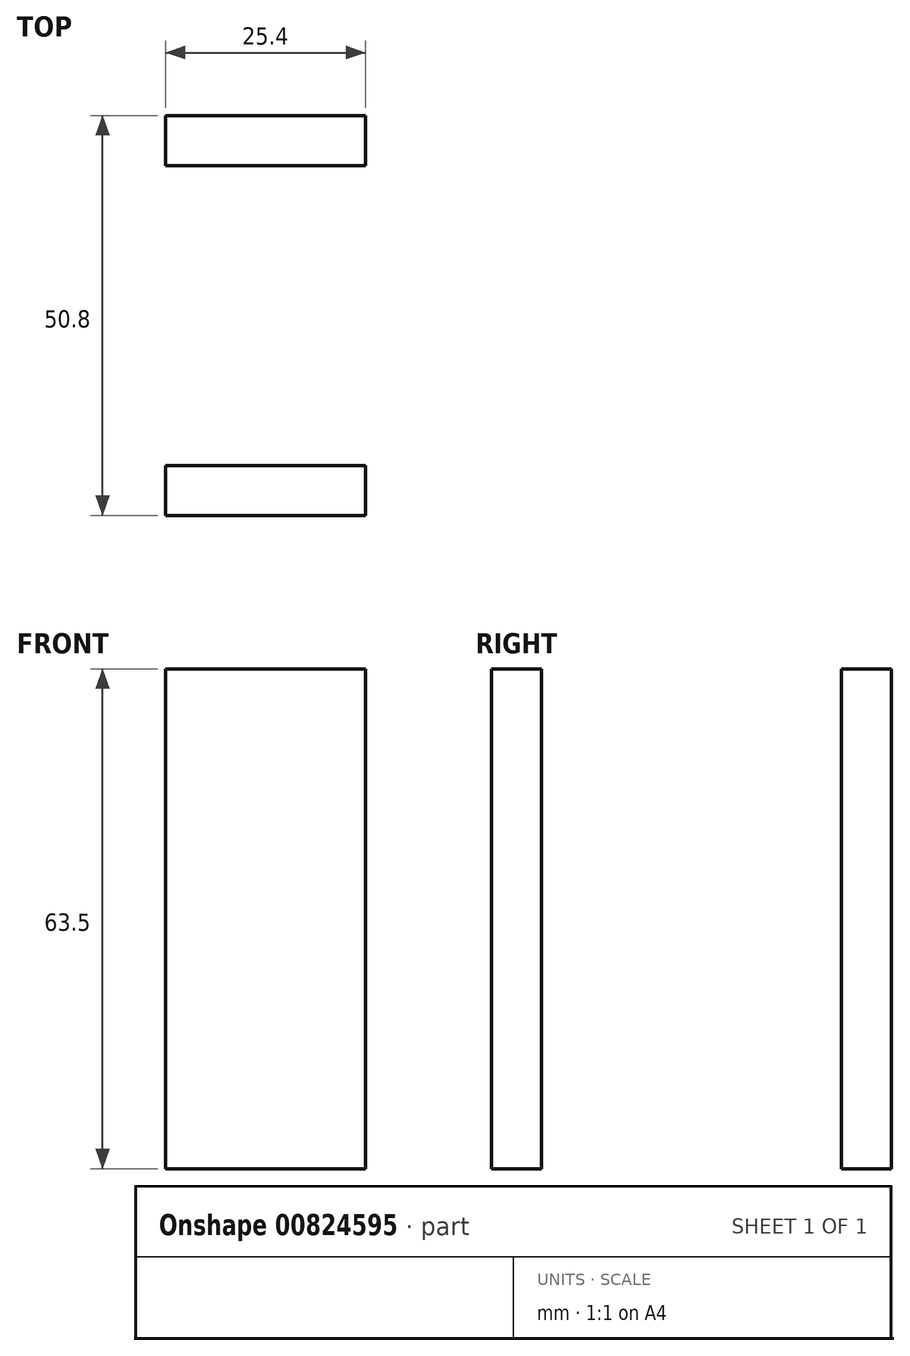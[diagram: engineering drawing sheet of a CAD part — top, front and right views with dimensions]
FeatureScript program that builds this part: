
annotation { "Feature Type Name" : "Feature", "Feature Type Description" : "" }
export const myFeature = defineFeature(function(context is Context, id is Id, definition is map)
    precondition{}
    {
        {
            var Q0;
            Q0=qCreatedBy(makeId("Right.planeOp"),FACE);
            var sketch = newSketch(context, id + "F0", { "sketchPlane" : qUnion([Q0])});
            skLineSegment(sketch, "E0", {"start": v(0, 0) * mm, "end": v(50.8, 0) * mm});
            skLineSegment(sketch, "E1", {"start": v(0, 0) * mm, "end": v(0, -76.2) * mm});
            skLineSegment(sketch, "E2", {"start": v(0, -76.2) * mm, "end": v(50.8, -76.2) * mm});
            skLineSegment(sketch, "E3", {"start": v(50.8, 0) * mm, "end": v(50.8, -76.2) * mm});
            skSolve(sketch);
        }
        {
            var Q0;
            Q0=makeQuery(id+"F0.imprint","IMPRINT",FACE,{"disambiguationData":[TD([[makeQuery(id+"F0.imprint","IMPRINT",EDGE,{"derivedFrom":sQuery(id+"F0.wireOp",EDGE,"E0")}),-1.0]])]});
            extrude(context, id + "F1", {"entities" : qUnion([Q0]), "depth" : 38.1 * mm, "offsetDistance" : 25.4 * mm});
        }
        {
            var Q0;
            Q0=makeQuery(id+"F1.opExtrude","SWEPT_FACE",FACE,{"disambiguationData":[OSD([sQuery(id+"F0.wireOp",EDGE,"E2")])]});
            var sketch = newSketch(context, id + "F2", { "sketchPlane" : qUnion([Q0])});
            skLineSegment(sketch, "E4", {"start": v(0, 0) * mm, "end": v(0, -50.8) * mm});
            skLineSegment(sketch, "E5", {"start": v(0, 0) * mm, "end": v(0, -6.35) * mm});
            skLineSegment(sketch, "E6", {"start": v(0, -6.35) * mm, "end": v(31.75, -6.35) * mm});
            skLineSegment(sketch, "E7", {"start": v(31.75, -6.35) * mm, "end": v(31.75, -44.45) * mm});
            skLineSegment(sketch, "E8", {"start": v(38.1, -50.8) * mm, "end": v(38.1, -44.45) * mm});
            skLineSegment(sketch, "E9", {"start": v(38.1, -44.45) * mm, "end": v(38.1, -50.8) * mm});
            skLineSegment(sketch, "E10", {"start": v(31.75, -44.45) * mm, "end": v(6.35, -44.45) * mm});
            skLineSegment(sketch, "E11", {"start": v(0, -6.35) * mm, "end": v(6.35, -6.35) * mm});
            skLineSegment(sketch, "E12", {"start": v(6.35, -6.35) * mm, "end": v(6.35, -44.45) * mm});
            skSolve(sketch);
        }
        {
            var Q0;
            Q0=makeQuery(id+"F2.imprint","IMPRINT",FACE,{"disambiguationData":[TD([[makeQuery(id+"F2.imprint","IMPRINT",EDGE,{"derivedFrom":sQuery(id+"F2.wireOp",EDGE,"E6")}),-1.0]])]});
            extrude(context, id + "F3", {"entities" : qUnion([Q0]), "operationType" : NewBodyOperationType.REMOVE, "oppositeDirection" : true, "depth" : 63.5 * mm, "offsetDistance" : 25.4 * mm});
        }
        {
            var Q0;
            Q0=makeQuery(id+"F1.opExtrude","SWEPT_FACE",FACE,{"disambiguationData":[OSD([sQuery(id+"F0.wireOp",EDGE,"E3")])]});
            var sketch = newSketch(context, id + "F4", { "sketchPlane" : qUnion([Q0])});
            skLineSegment(sketch, "E13", {"start": v(-38.1, -76.2) * mm, "end": v(0, -76.2) * mm});
            skLineSegment(sketch, "E14", {"start": v(-38.1, -76.2) * mm, "end": v(-31.75, -76.2) * mm});
            skLineSegment(sketch, "E15", {"start": v(0, -76.2) * mm, "end": v(-6.35, -76.2) * mm});
            skLineSegment(sketch, "E16", {"start": v(-31.75, -76.2) * mm, "end": v(-31.75, -12.7) * mm});
            skLineSegment(sketch, "E17", {"start": v(-38.1, -76.2) * mm, "end": v(-38.1, 0) * mm});
            skLineSegment(sketch, "E18", {"start": v(-31.75, -12.7) * mm, "end": v(-6.35, -12.7) * mm});
            skLineSegment(sketch, "E19", {"start": v(-6.35, -12.7) * mm, "end": v(-6.35, -76.2) * mm});
            skSolve(sketch);
        }
        {
            var Q0;
            Q0=makeQuery(id+"F1.opExtrude","CAP_FACE",FACE,{"disambiguationData":[OSD([sQuery(id+"F0.wireOp",EDGE,"E0"),sQuery(id+"F0.wireOp",EDGE,"E1"),sQuery(id+"F0.wireOp",EDGE,"E2"),sQuery(id+"F0.wireOp",EDGE,"E3")])],"isStart":false});
            var sketch = newSketch(context, id + "F5", { "sketchPlane" : qUnion([Q0])});
            skLineSegment(sketch, "E20", {"start": v(0, 0) * mm, "end": v(50.8, 0) * mm});
            skSolve(sketch);
        }
        {
            var Q0;
            Q0=makeQuery(id+"F4.imprint","IMPRINT",FACE,{"disambiguationData":[TD([[makeQuery(id+"F4.imprint","IMPRINT",EDGE,{"derivedFrom":sQuery(id+"F4.wireOp",EDGE,"E13")}),1.0]])]});
            extrude(context, id + "F6", {"entities" : qUnion([Q0]), "operationType" : NewBodyOperationType.REMOVE, "oppositeDirection" : true, "depth" : 50.8 * mm, "offsetDistance" : 25.4 * mm});
        }
    });
